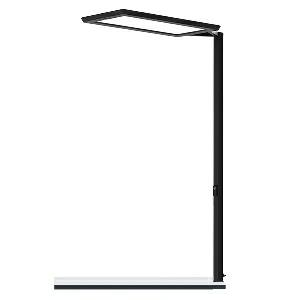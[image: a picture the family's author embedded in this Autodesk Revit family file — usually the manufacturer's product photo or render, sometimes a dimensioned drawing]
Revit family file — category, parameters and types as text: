
# Revit family: yara_single_-_yat_15000_vtl_r_sw_cee_00_00810195_2b29
name_source: partatom
category: Lighting Fixtures
units: mm (PartAtom-declared; Revit-internal decimal feet)

## family parameters
Cut with Voids When Loaded = No
Host = Face
Light Source = No
Part Type = Normal
Room Calculation Point = No
Round Connector Dimension = Use Diameter
Shared = No

## types (1)
- YARA.single - YAT 15000/VTL/R/SW/CEE/00 (1 x LED, 15000 lm, VTL)
    Apparent Load = 107 VA
    Approval mark = CE
    CIE Flux Codes = 58 87 97 13 100
    Color Rendering = 80-89
    Color Temperature = VTL
    Control Gear = Electronic ballast
    Default Elevation = 1800 mm
    Description = YAT 15000/VTL/R/SW/CEE/00/|Desk-mounted luminaire|light source: LED|work equipment: Electronic ballast DALI|connected load: 220-240 V, 50/60 Hz|Power consumption: approx. 107 W|standby: approx. 0,50|power factor: approx. 0,966|luminous flux: 15000 lm|luminous efficacy: 140 lm/W|light distribution: Direct/indirect|direct ratio: approx. 13 %|colour temperature: Daylight, ca. 2700-6500 K|color rendering index (CRI): >= 80|chromaticity tolerance:  3 SDCM|technology: Presence and daylight sensor control (PIR)|operation: Wireless switch|luminaire body|material: Aluminium/plastic|surface: Powder coatet|colour: Black|lamp cover: Acrylic (PMMA), Satine, Structured|tubular section|material: Steel tube|surface: Powder-coated|Form: Tubular section upright|colour of tubular section: Black|weight (net): approx. 7.7 kg|mains lead: 3.00 m Mains plug CEE 7/VII|Fastening: Socket, Table adaptor|glare control: Prism aperture|luminance(L65): <= 2700 cd/m|unified glare rating(4H 8H): <=  16|special features: App control, Asymmetric radiation, Biodynamic light VTL, Direct and indirect lighting component with edge light and light guidetechnology for a homogeneous light exit, Flicker-free, Magnetic control panel, freely positionable, PIR movement and daylight sensor|Approval mark: VDE - ENEC|
    Frequency = 50 Hz, 60 Hz
    Height = 24 mm  [stored 0.0787402 ft]
    Lamp = 1 x LED
    Lamp Light Flux = 15000 lm
    Lamp count = 1
    Length = 690 mm
    Luminous efficacy = 140 lm/W
    Manufacturer = Waldmann
    ModVariant = No
    Model = 00810195
    Mounting Place = Table
    Mounting Type = Surface mounted
    Number of Poles = 1
    OnlyDefault = Yes
    Power Factor = 1
    Product Name = YARA.single - YAT 15000/VTL/R/SW/CEE/00
    Product group = Desk mounted luminaire
    ProductGroupID = 22
    Protection Class = Protection class I
    Protection Degree = IP 20
    RLX_Detail_Level = 1
    RLX_Emergency_Light_Flux = 0 lm
    RLX_Emergency_Type = 0
    RLX_Emergency_Type_DB = No
    RlxData = <blob elided: 61873 chars, md5=28f3e4c3>
    Socket = socket
    Standby Power = 0 W
    System Light Flux = 15000 lm
    System Power = 107 W
    Type Comments = Product without accessories
    Type Image = yat-r-sw.jpg
    URL = http://relux.com
    VarID = ---
    Voltage = 230 V
    Voltage Range = 220-240 V
    Weight = 0.00 kg
    Width = 358 mm

note: [stored X ft] marks values corroborated as IEEE doubles in the binary element streams (Revit-internal decimal feet)

## geometry (parser evidence)
native form markers: Blend x4, Sweep x14
no freeform markers — native parametric forms only
